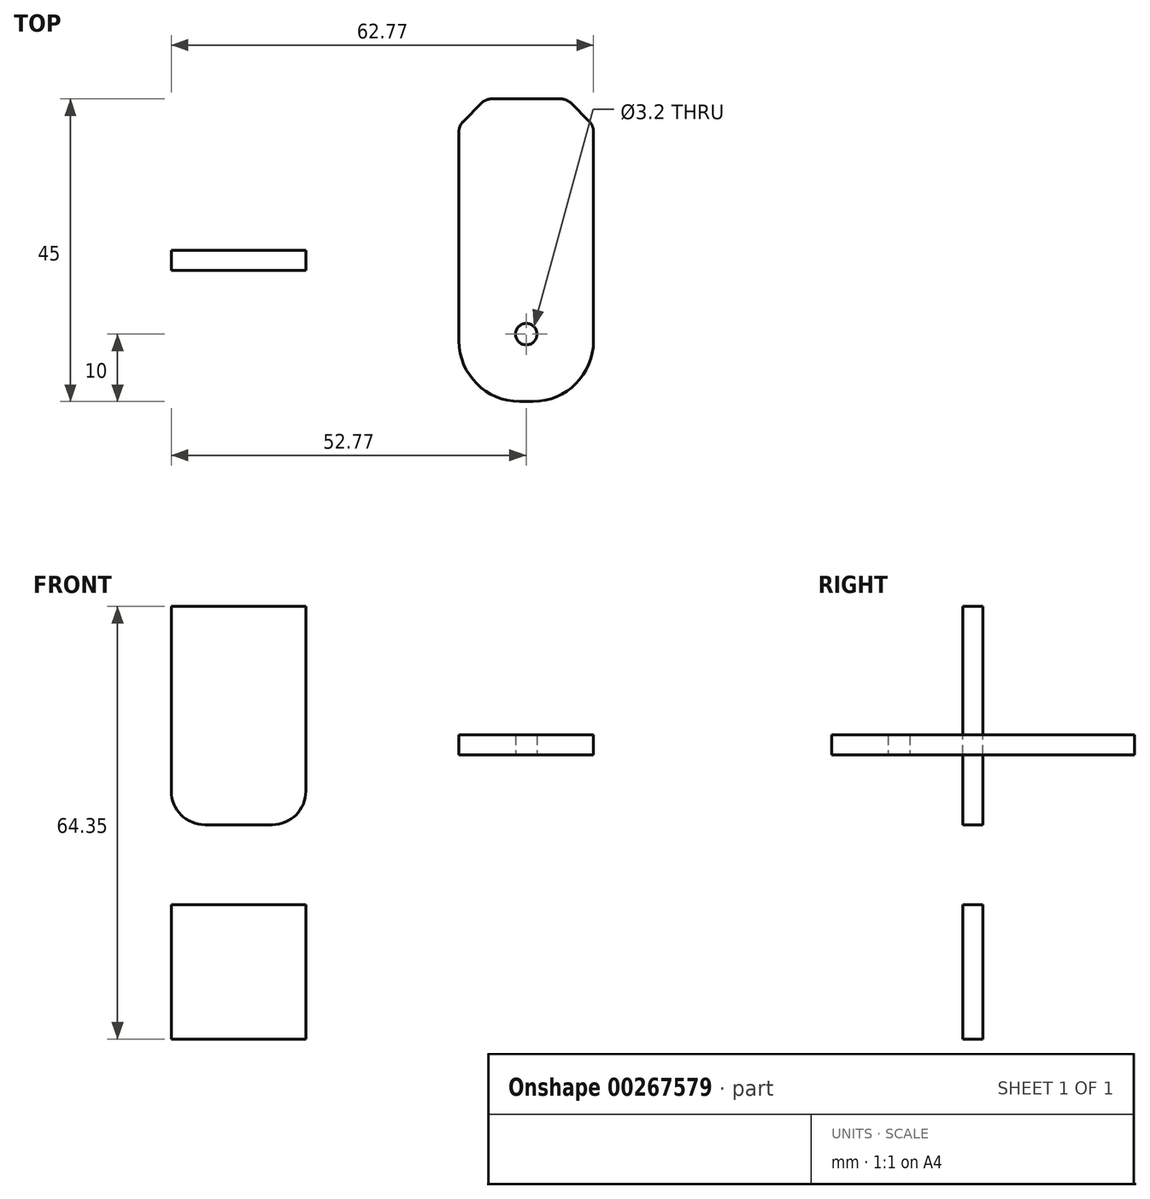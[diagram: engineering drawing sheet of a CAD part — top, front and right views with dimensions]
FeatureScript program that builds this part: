
annotation { "Feature Type Name" : "Feature", "Feature Type Description" : "" }
export const myFeature = defineFeature(function(context is Context, id is Id, definition is map)
    precondition{}
    {
        {
            var Q0;
            Q0=qCreatedBy(makeId("Top.planeOp"),FACE);
            var sketch = newSketch(context, id + "F0", { "sketchPlane" : qUnion([Q0])});
            skLineSegment(sketch, "E0.bottom", {"start": v(10, 22.5) * mm, "end": v(-10, 22.5) * mm});
            skLineSegment(sketch, "E0.top", {"start": v(10, -22.5) * mm, "end": v(-10, -22.5) * mm});
            skLineSegment(sketch, "E0.left", {"start": v(10, 22.5) * mm, "end": v(10, -22.5) * mm});
            skLineSegment(sketch, "E0.right", {"start": v(-10, 22.5) * mm, "end": v(-10, -22.5) * mm});
            skPoint(sketch, "E0.middle", {"position": v(0, 0) * mm});
            skCircle(sketch, "E1", {"center": v(0, -12.5) * mm, "radius": 1.6 * mm});
            skCircle(sketch, "E2", {"center": v(0, -12.5) * mm, "radius": 10 * mm, "construction": true});
            skSolve(sketch);
        }
        {
            var Q0;
            Q0=qSketchRegion(id+"F0",true);
            extrude(context, id + "F1", {"entities" : qUnion([Q0]), "depth" : 3 * mm});
        }
        {
            var Q0;
            Q0=makeQuery(id+"F1.opExtrude","SWEPT_EDGE",EDGE,{"disambiguationData":[OSD([sQuery(id+"F0.wireOp",EDGE,"E0.top"),sQuery(id+"F0.wireOp",EDGE,"E0.left")])]});
            var Q1;
            Q1=makeQuery(id+"F1.opExtrude","SWEPT_EDGE",EDGE,{"disambiguationData":[OSD([sQuery(id+"F0.wireOp",EDGE,"E0.top"),sQuery(id+"F0.wireOp",EDGE,"E0.right")])]});
            fillet(context, id + "F2", {"entities" : qUnion([Q0, Q1]), "radius" : 9 * mm, "tangentPropagation" : true, "allowEdgeOverflow" : false});
        }
        {
            var Q0;
            Q0=makeQuery(id+"F1.opExtrude","SWEPT_EDGE",EDGE,{"disambiguationData":[OSD([sQuery(id+"F0.wireOp",EDGE,"E0.bottom"),sQuery(id+"F0.wireOp",EDGE,"E0.right")])]});
            var Q1;
            Q1=makeQuery(id+"F1.opExtrude","SWEPT_EDGE",EDGE,{"disambiguationData":[OSD([sQuery(id+"F0.wireOp",EDGE,"E0.bottom"),sQuery(id+"F0.wireOp",EDGE,"E0.left")])]});
            chamfer(context, id + "F3", {"entities" : qUnion([Q0, Q1]), "width" : 4 * mm, "tangentPropagation" : true});
        }
        {
            var Q0;
            {var subQ0=sQuery(id+"F0.wireOp",EDGE,"E0.bottom");Q0=makeQuery(id+"F3.opChamfer","BLEND_EDGE",EDGE,{"blendedFrom":[makeQuery(id+"F1.opExtrude","SWEPT_EDGE",EDGE,{"disambiguationData":[OSD([subQ0,sQuery(id+"F0.wireOp",EDGE,"E0.right")])]}),makeQuery(id+"F1.opExtrude","SWEPT_FACE",FACE,{"disambiguationData":[OSD([subQ0])]})],"blendedInto":[makeQuery(id+"F1.opExtrude","SWEPT_FACE",FACE,{"disambiguationData":[OSD([subQ0])]})]});}
            var Q1;
            {var subQ0=sQuery(id+"F0.wireOp",EDGE,"E0.bottom");Q1=makeQuery(id+"F3.opChamfer","BLEND_EDGE",EDGE,{"blendedFrom":[makeQuery(id+"F1.opExtrude","SWEPT_EDGE",EDGE,{"disambiguationData":[OSD([subQ0,sQuery(id+"F0.wireOp",EDGE,"E0.left")])]}),makeQuery(id+"F1.opExtrude","SWEPT_FACE",FACE,{"disambiguationData":[OSD([subQ0])]})],"blendedInto":[makeQuery(id+"F1.opExtrude","SWEPT_FACE",FACE,{"disambiguationData":[OSD([subQ0])]})]});}
            var Q2;
            {var subQ0=sQuery(id+"F0.wireOp",EDGE,"E0.left");Q2=makeQuery(id+"F3.opChamfer","BLEND_EDGE",EDGE,{"blendedFrom":[makeQuery(id+"F1.opExtrude","SWEPT_EDGE",EDGE,{"disambiguationData":[OSD([sQuery(id+"F0.wireOp",EDGE,"E0.bottom"),subQ0])]}),makeQuery(id+"F1.opExtrude","SWEPT_FACE",FACE,{"disambiguationData":[OSD([subQ0])]})],"blendedInto":[makeQuery(id+"F1.opExtrude","SWEPT_FACE",FACE,{"disambiguationData":[OSD([subQ0])]})]});}
            var Q3;
            {var subQ0=sQuery(id+"F0.wireOp",EDGE,"E0.right");Q3=makeQuery(id+"F3.opChamfer","BLEND_EDGE",EDGE,{"blendedFrom":[makeQuery(id+"F1.opExtrude","SWEPT_EDGE",EDGE,{"disambiguationData":[OSD([sQuery(id+"F0.wireOp",EDGE,"E0.bottom"),subQ0])]}),makeQuery(id+"F1.opExtrude","SWEPT_FACE",FACE,{"disambiguationData":[OSD([subQ0])]})],"blendedInto":[makeQuery(id+"F1.opExtrude","SWEPT_FACE",FACE,{"disambiguationData":[OSD([subQ0])]})]});}
            fillet(context, id + "F4", {"entities" : qUnion([Q0, Q1, Q2, Q3]), "radius" : 2 * mm, "tangentPropagation" : true, "allowEdgeOverflow" : false});
        }
        {
            var Q0;
            Q0=qCreatedBy(makeId("Front.planeOp"),FACE);
            var sketch = newSketch(context, id + "F5", { "sketchPlane" : qUnion([Q0])});
            skLineSegment(sketch, "E3.bottom", {"start": v(-32.77, -42.25) * mm, "end": v(-52.77, -42.25) * mm});
            skLineSegment(sketch, "E3.top", {"start": v(-32.77, -22.25) * mm, "end": v(-52.77, -22.25) * mm});
            skLineSegment(sketch, "E3.left", {"start": v(-32.77, -42.25) * mm, "end": v(-32.77, -22.25) * mm});
            skLineSegment(sketch, "E3.right", {"start": v(-52.77, -42.25) * mm, "end": v(-52.77, -22.25) * mm});
            skPoint(sketch, "E3.middle", {"position": v(-42.77, -32.25) * mm});
            skLineSegment(sketch, "E4.bottom", {"start": v(-52.77, -10.37) * mm, "end": v(-32.77, -10.37) * mm});
            skLineSegment(sketch, "E4.top", {"start": v(-52.77, 22.1) * mm, "end": v(-32.77, 22.1) * mm});
            skLineSegment(sketch, "E4.left", {"start": v(-52.77, -10.37) * mm, "end": v(-52.77, 22.1) * mm});
            skLineSegment(sketch, "E4.right", {"start": v(-32.77, -10.37) * mm, "end": v(-32.77, 22.1) * mm});
            skSolve(sketch);
        }
        {
            var Q0;
            Q0=qSketchRegion(id+"F5",true);
            extrude(context, id + "F6", {"entities" : qUnion([Q0]), "depth" : 3 * mm});
        }
        {
            var Q0;
            Q0=makeQuery(id+"F6.opExtrude","SWEPT_EDGE",EDGE,{"disambiguationData":[OSD([sQuery(id+"F5.wireOp",EDGE,"E4.bottom"),sQuery(id+"F5.wireOp",EDGE,"E4.right")])]});
            var Q1;
            Q1=makeQuery(id+"F6.opExtrude","SWEPT_EDGE",EDGE,{"disambiguationData":[OSD([sQuery(id+"F5.wireOp",EDGE,"E4.bottom"),sQuery(id+"F5.wireOp",EDGE,"E4.left")])]});
            fillet(context, id + "F7", {"entities" : qUnion([Q0, Q1]), "radius" : 5 * mm, "tangentPropagation" : true, "allowEdgeOverflow" : false});
        }
    });
